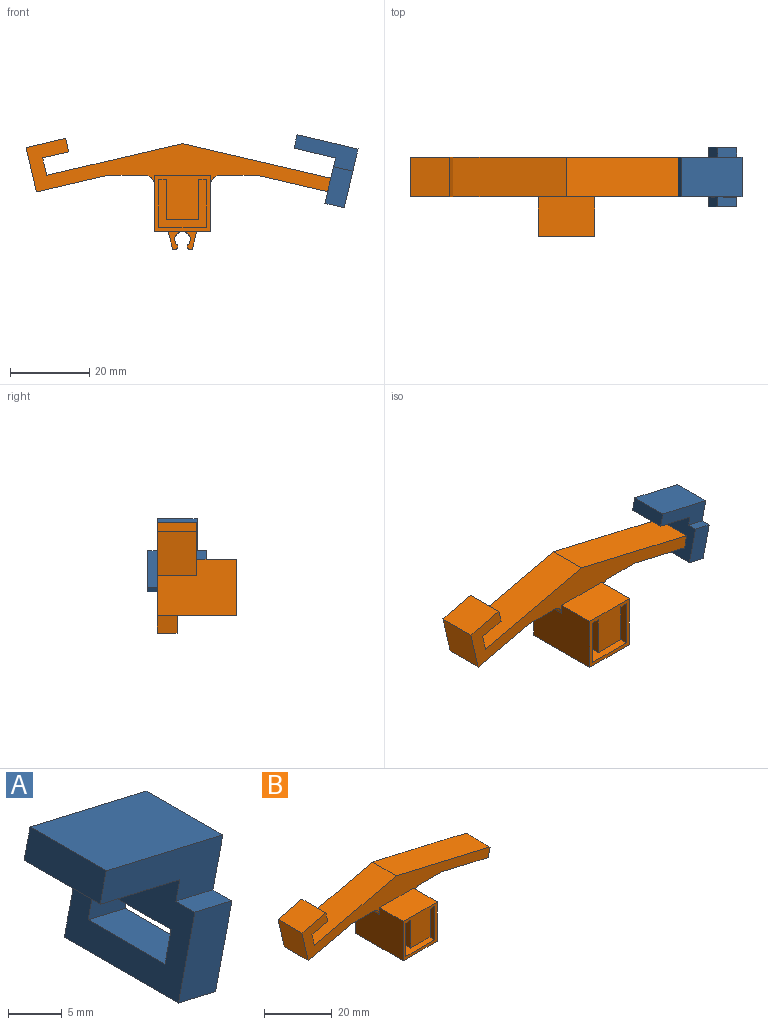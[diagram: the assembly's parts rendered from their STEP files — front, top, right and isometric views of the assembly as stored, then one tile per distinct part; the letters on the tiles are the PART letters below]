
ASSEMBLY  parts=2 mates=1
PART A: 16 faces, bbox 16.1x15x18.4 mm
  f0: plane 15x11.44mm, normal (-0.97,0,0.23), area 128.6mm2, adj f1,f2,f4,f5,f6,f7,f8,f9
  f1: plane 16.13x9.18mm, normal (0,-1,0), area 66.4mm2, adj f0,f3,f4,f5,f10,f15
  f2: plane 16.13x9.18mm, normal (0,1,0), area 66.4mm2, adj f0,f3,f4,f9,f10,f15
  f3: plane 15.34x10mm, normal (0.23,0,0.97), area 157.5mm2, adj f1,f2,f10,f15
  f4: plane 10.47x10mm, normal (-0.23,0,-0.97), area 107.5mm2, adj f0,f1,f2,f10
  f5: plane 4.87x2.5mm, normal (0.23,0,0.97), area 12.5mm2, adj f0,f1,f6,f15
  f6: plane 10.39x7.03mm, normal (0,-1,0), area 47.5mm2, adj f0,f5,f7,f15
  f7: plane 15x4.87mm, normal (-0.23,0,-0.97), area 75mm2, adj f0,f6,f8,f15
  f8: plane 10.39x7.03mm, normal (0,1,0), area 47.5mm2, adj f0,f7,f9,f15
  f9: plane 4.87x2.5mm, normal (0.23,0,0.97), area 12.5mm2, adj f0,f2,f8,f15
  f10: plane 10x3.41mm, normal (-0.97,0,0.23), area 35mm2, adj f1,f2,f3,f4
  f11: plane 10.1x4.87mm, normal (0.23,0,0.97), area 50.5mm2, adj f0,f12,f14,f15
  f12: plane 5.69x4.64mm, normal (0,-1,0), area 18mm2, adj f0,f11,f13,f15
  f13: plane 10.1x4.87mm, normal (-0.23,0,-0.97), area 50.5mm2, adj f0,f12,f14,f15
  f14: plane 5.69x4.64mm, normal (0,1,0), area 18mm2, adj f0,f11,f13,f15
  f15: plane 15x14.85mm, normal (0.97,0,-0.23), area 163.6mm2, adj f1,f2,f3,f5,f6,f7,f8,f9
PART B: 41 faces, bbox 78.6x20x28 mm
  f0: plane 10x9.26mm, normal (0,0,-1), area 92.6mm2, adj f6,f11,f12,f39
  f1: plane 10x4.38mm, normal (0.97,0,0.23), area 45mm2, adj f2,f10,f11,f12
  f2: plane 10x6.57mm, normal (0.23,0,-0.97), area 67.5mm2, adj f1,f3,f11,f12
  f3: plane 10x3.41mm, normal (0.97,0,0.23), area 35mm2, adj f2,f4,f11,f12
  f4: plane 10x9.98mm, normal (-0.23,0,0.97), area 102.5mm2, adj f3,f5,f11,f12
  f5: plane 11.2x10mm, normal (-0.97,0,-0.23), area 115mm2, adj f4,f6,f11,f12
  f6: plane 18x10mm, normal (0.23,0,-0.97), area 184.8mm2, adj f0,f5,f11,f12
  f7: plane 10x9.26mm, normal (0,0,-1), area 92.6mm2, adj f8,f11,f12,f40
  f8: plane 19.46x10mm, normal (-0.23,0,-0.97), area 199.8mm2, adj f7,f11,f12,f13
  f9: plane 39.12x10mm, normal (0.23,0,0.97), area 401.7mm2, adj f10,f11,f12,f13
  f10: plane 34.25x10mm, normal (-0.23,0,0.97), area 351.7mm2, adj f1,f9,f11,f12
  f11: plane 78.6x13.87mm, normal (0,-1,0), area 410.5mm2, adj f0,f1,f2,f3,f4,f5,f6,f7
  f12: plane 78.6x27.98mm, normal (0,1,0), area 625.6mm2, adj f0,f1,f2,f3,f4,f5,f6,f7
  f13: plane 10x3.41mm, normal (0.97,0,-0.23), area 35mm2, adj f8,f9,f11,f12
  f14: plane 14.2x10mm, normal (0,0,1), area 142mm2, adj f11,f15,f25,f26
  f15: plane 20x14.2mm, normal (-1,0,0), area 259mm2, adj f11,f12,f14,f16,f26,f39
  f16: plane 20x14.2mm, normal (0,0,-1), area 248mm2, adj f12,f15,f25,f26,f29,f32,f33,f36
  f17: plane 15x2mm, normal (0,0,-1), area 30mm2, adj f18,f24,f26,f27
  f18: plane 15x10.1mm, normal (-1,0,0), area 151.5mm2, adj f17,f19,f26,f27
  f19: plane 15x8.1mm, normal (0,0,-1), area 121.5mm2, adj f18,f20,f26,f27
  f20: plane 15x10.1mm, normal (1,0,0), area 151.5mm2, adj f19,f21,f26,f27
  f21: plane 15x2mm, normal (0,0,-1), area 30mm2, adj f20,f22,f26,f27
  f22: plane 15x12.1mm, normal (-1,0,0), area 181.5mm2, adj f21,f23,f26,f27
  f23: plane 15x12.1mm, normal (0,0,1), area 181.5mm2, adj f22,f24,f26,f27
  f24: plane 15x12.1mm, normal (1,0,0), area 181.5mm2, adj f17,f23,f26,f27
  f25: plane 20x14.2mm, normal (1,0,0), area 259mm2, adj f11,f12,f14,f16,f26,f40
  f26: plane 14.2x14.2mm, normal (0,-1,0), area 137mm2, adj f14,f15,f16,f17,f18,f19,f20,f21
  f27: plane 12.1x12.1mm, normal (0,-1,0), area 64.6mm2, adj f17,f18,f19,f20,f21,f22,f23,f24
  f28: plane 5x0.8mm, normal (0,0,-1), area 4mm2, adj f12,f29,f32,f38
  f29: plane 5x4.45mm, normal (-0.97,0,-0.24), area 22.9mm2, adj f12,f16,f28,f32
  f30: cylinder r=1.95mm len=5mm, axis (0,1,0), area 48.3mm2, adj f12,f31,f32,f35,f36
  f31: plane 5x0.46mm, normal (1,0,0), area 2.3mm2, adj f12,f30,f32,f38
  f32: plane 4.45x3.6mm, normal (0,-1,0), area 6.7mm2, adj f16,f28,f29,f30,f31,f38
  f33: plane 5x4.45mm, normal (0.97,0,-0.24), area 22.9mm2, adj f12,f16,f34,f36
  f34: plane 5x0.8mm, normal (0,0,-1), area 4mm2, adj f12,f33,f36,f37
  f35: plane 5x0.46mm, normal (-1,0,0), area 2.3mm2, adj f12,f30,f36,f37
  f36: plane 4.45x3.6mm, normal (0,-1,0), area 6.7mm2, adj f16,f30,f33,f34,f35,f37
  f37: cylinder r=0.5mm len=5mm, axis (0,-1,0), area 3.9mm2, adj f12,f34,f35,f36
  f38: cylinder r=0.5mm len=5mm, axis (0,1,0), area 3.9mm2, adj f12,f28,f31,f32
  f39: cylinder r=2.5mm len=10mm, axis (0,1,0), area 39.3mm2, adj f0,f11,f12,f15
  f40: cylinder r=2.5mm len=10mm, axis (0,-1,0), area 39.3mm2, adj f7,f11,f12,f25
PLACE A t=(3.34,-0.05,-0.01)mm
PLACE B at identity
MATE parallel A.f12 <-> B.f12  axis (0,-1,0) through (39.45,5,-3.01)mm
